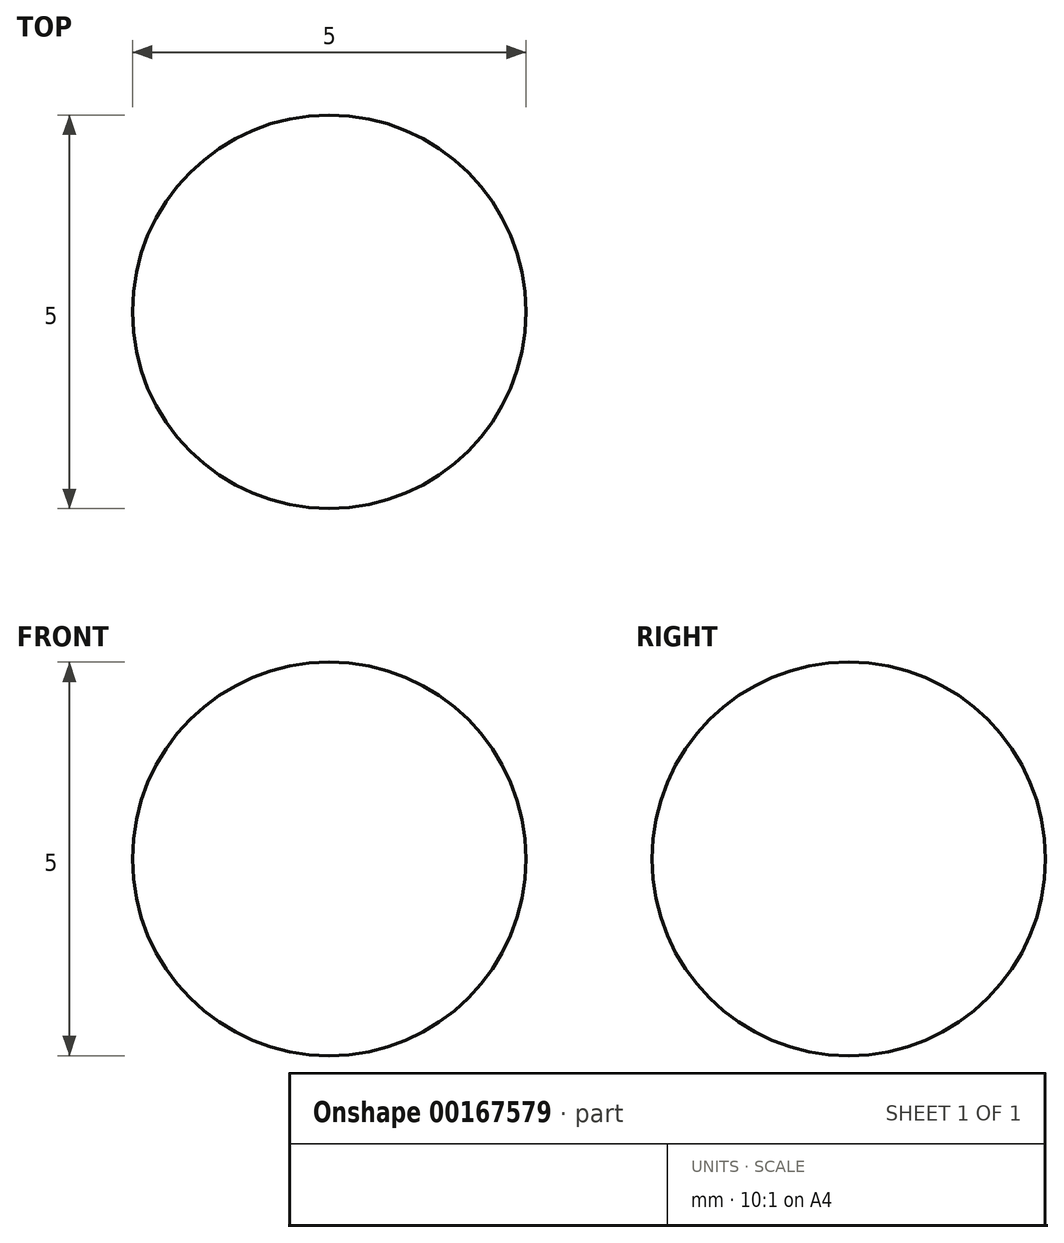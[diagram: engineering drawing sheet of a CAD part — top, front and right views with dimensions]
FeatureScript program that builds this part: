
annotation { "Feature Type Name" : "Feature", "Feature Type Description" : "" }
export const myFeature = defineFeature(function(context is Context, id is Id, definition is map)
    precondition{}
    {
        {
            var Q0;
            Q0=qCreatedBy(makeId("Front.planeOp"),FACE);
            var sketch = newSketch(context, id + "F0", { "sketchPlane" : qUnion([Q0])});
            skCircle(sketch, "E0", {"center": v(0, 0) * mm, "radius": 2.5 * mm});
            skLineSegment(sketch, "E1", {"start": v(-2.5, 0) * mm, "end": v(2.5, 0) * mm});
            skSolve(sketch);
        }
        {
            var Q0;
            {var subQ0=sQuery(id+"F0.wireOp",EDGE,"E1");Q0=makeQuery(id+"F0.imprint","IMPRINT",FACE,{"disambiguationData":[TD([[makeQuery(id+"F0.imprint","IMPRINT",EDGE,{"derivedFrom":subQ0}),1.0]])]});}
            var Q1;
            Q1=sQuery(id+"F0.wireOp",EDGE,"E1");
            revolve(context, id + "F1", {"entities" : qUnion([Q0]), "axis" : qUnion([Q1]), "revolveType" : RevolveType.FULL});
        }
    });
